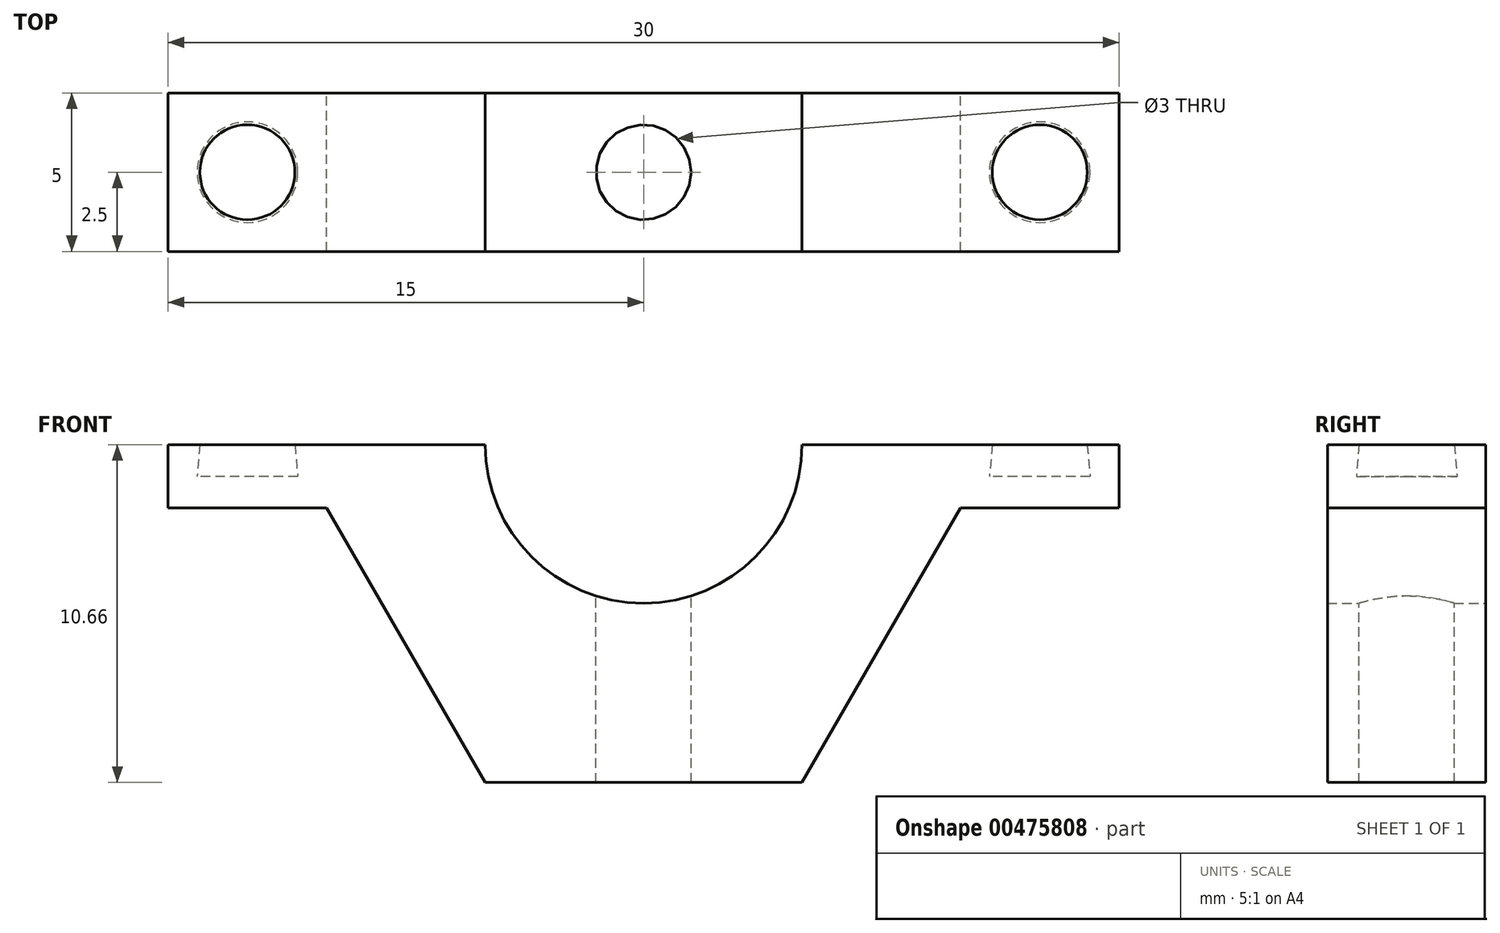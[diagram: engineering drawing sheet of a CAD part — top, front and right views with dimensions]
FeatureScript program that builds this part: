
annotation { "Feature Type Name" : "Feature", "Feature Type Description" : "" }
export const myFeature = defineFeature(function(context is Context, id is Id, definition is map)
    precondition{}
    {
        {
            var Q0;
            Q0=qCreatedBy(makeId("Front.planeOp"),FACE);
            var sketch = newSketch(context, id + "F0", { "sketchPlane" : qUnion([Q0])});
            skArc(sketch, "E0", {"start": v(-5, 0) * mm, "mid": v(-3.54, -3.54) * mm, "end": v(0, -5) * mm});
            skLineSegment(sketch, "E1", {"start": v(-5, -10.66) * mm, "end": v(0, -10.66) * mm});
            skLineSegment(sketch, "E2", {"start": v(-5, -10.66) * mm, "end": v(-10, -2) * mm});
            skLineSegment(sketch, "E3", {"start": v(-10, -2) * mm, "end": v(-15, -2) * mm});
            skLineSegment(sketch, "E4", {"start": v(-15, -2) * mm, "end": v(-15, 0) * mm});
            skLineSegment(sketch, "E5", {"start": v(-15, 0) * mm, "end": v(-5, 0) * mm});
            skLineSegment(sketch, "E6", {"start": v(0, -10.66) * mm, "end": v(0, 0) * mm, "construction": true});
            skLineSegment(sketch, "E7.MirrorCS", {"start": v(15, 0) * mm, "end": v(5, 0) * mm});
            skLineSegment(sketch, "E8.MirrorCS", {"start": v(10, -2) * mm, "end": v(15, -2) * mm});
            skLineSegment(sketch, "E9.MirrorCS", {"start": v(15, -2) * mm, "end": v(15, 0) * mm});
            skArc(sketch, "E10.MirrorCS", {"start": v(5, 0) * mm, "mid": v(3.54, -3.54) * mm, "end": v(0, -5) * mm});
            skLineSegment(sketch, "E11.MirrorCS", {"start": v(5, -10.66) * mm, "end": v(0, -10.66) * mm});
            skLineSegment(sketch, "E12.MirrorCS", {"start": v(5, -10.66) * mm, "end": v(10, -2) * mm});
            skSolve(sketch);
        }
        {
            var Q0;
            Q0=makeQuery(id+"F0.imprint","IMPRINT",FACE,{"disambiguationData":[TD([[makeQuery(id+"F0.imprint","IMPRINT",EDGE,{"derivedFrom":sQuery(id+"F0.wireOp",EDGE,"E0")}),-1.0]])]});
            extrude(context, id + "F1", {"entities" : qUnion([Q0]), "endBound" : BoundingType.SYMMETRIC, "depth" : 5 * mm, "offsetDistance" : 25 * mm});
        }
        {
            var Q0;
            Q0=makeQuery(id+"F1.opExtrude","SWEPT_FACE",FACE,{"disambiguationData":[OSD([sQuery(id+"F0.wireOp",EDGE,"E7.MirrorCS")])]});
            cPlane(context, id + "F2", {"entities" : qUnion([Q0]), "cplaneType" : CPlaneType.OFFSET, "offset" : 0 * mm, "width" : 150 * mm, "height" : 150 * mm});
        }
        {
            var Q0;
            Q0=qCreatedBy(id+"F2.planeOp",FACE);
            var sketch = newSketch(context, id + "F3", { "sketchPlane" : qUnion([Q0])});
            skCircle(sketch, "E13", {"center": v(12.5, 0) * mm, "radius": 1.5 * mm});
            skCircle(sketch, "E14", {"center": v(-12.5, 0) * mm, "radius": 1.5 * mm});
            skCircle(sketch, "E15", {"center": v(0, 0) * mm, "radius": 1.5 * mm});
            skSolve(sketch);
        }
        {
            var Q0;
            Q0=makeQuery(id+"F3.imprint","IMPRINT",FACE,{"disambiguationData":[TD([[makeQuery(id+"F3.imprint","IMPRINT",EDGE,{"derivedFrom":sQuery(id+"F3.wireOp",EDGE,"E14")}),1.0]])]});
            var Q1;
            Q1=makeQuery(id+"F3.imprint","IMPRINT",FACE,{"disambiguationData":[TD([[makeQuery(id+"F3.imprint","IMPRINT",EDGE,{"derivedFrom":sQuery(id+"F3.wireOp",EDGE,"E13")}),1.0]])]});
            extrude(context, id + "F4", {"entities" : qUnion([Q0, Q1]), "operationType" : NewBodyOperationType.REMOVE, "oppositeDirection" : true, "depth" : 1 * mm, "offsetDistance" : 25 * mm, "hasDraft" : true, "draftAngle" : 5 * degree});
        }
        {
            var Q0;
            Q0=makeQuery(id+"F3.imprint","IMPRINT",FACE,{"disambiguationData":[TD([[makeQuery(id+"F3.imprint","IMPRINT",EDGE,{"derivedFrom":sQuery(id+"F3.wireOp",EDGE,"E15")}),1.0]])]});
            extrude(context, id + "F5", {"entities" : qUnion([Q0]), "operationType" : NewBodyOperationType.REMOVE, "oppositeDirection" : true, "depth" : 25 * mm, "offsetDistance" : 25 * mm});
        }
    });
